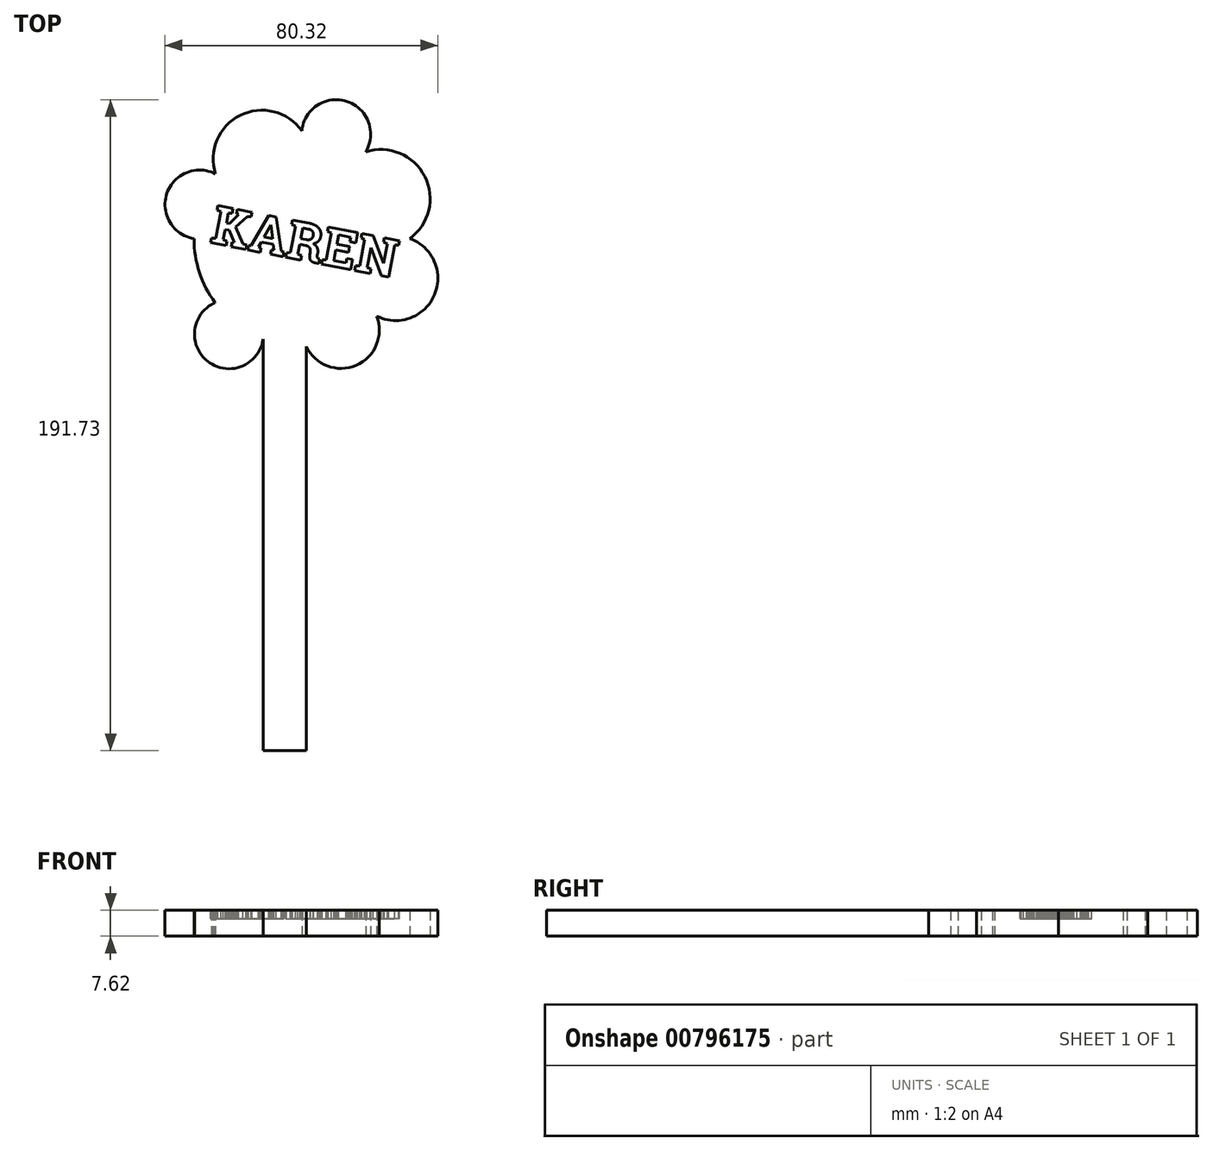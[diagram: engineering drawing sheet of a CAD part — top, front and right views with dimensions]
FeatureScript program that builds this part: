
annotation { "Feature Type Name" : "Feature", "Feature Type Description" : "" }
export const myFeature = defineFeature(function(context is Context, id is Id, definition is map)
    precondition{}
    {
        {
            var Q0;
            Q0=qCreatedBy(makeId("Top.planeOp"),FACE);
            var sketch = newSketch(context, id + "F0", { "sketchPlane" : qUnion([Q0])});
            skLineSegment(sketch, "E0.bottom", {"start": v(-11.4, 1.6) * mm, "end": v(1.3, 1.6) * mm});
            skLineSegment(sketch, "E0.top", {"start": v(-11.4, -150.8) * mm, "end": v(1.3, -150.8) * mm});
            skLineSegment(sketch, "E0.left", {"start": v(-11.4, 1.6) * mm, "end": v(-11.4, -150.8) * mm});
            skLineSegment(sketch, "E0.right", {"start": v(1.3, 1.6) * mm, "end": v(1.3, -150.8) * mm});
            skCircle(sketch, "E1", {"center": v(0, 0) * mm, "radius": 31.75 * mm});
            skArc(sketch, "E2", {"start": v(-25.54, -18.87) * mm, "mid": v(-27.6, -36.25) * mm, "end": v(-11.4, -29.64) * mm});
            skArc(sketch, "E3", {"start": v(-31.75, 0) * mm, "mid": v(-40.33, -13.28) * mm, "end": v(-25.54, -18.87) * mm});
            skArc(sketch, "E4", {"start": v(-25.41, 19.03) * mm, "mid": v(-39.75, 13.24) * mm, "end": v(-31.75, 0) * mm});
            skArc(sketch, "E5", {"start": v(0, 31.75) * mm, "mid": v(-18.16, 36.29) * mm, "end": v(-25.41, 19.03) * mm});
            skArc(sketch, "E6", {"start": v(18.84, 25.56) * mm, "mid": v(13.28, 40.42) * mm, "end": v(0, 31.75) * mm});
            skArc(sketch, "E7", {"start": v(31.75, 0) * mm, "mid": v(36.21, 18.3) * mm, "end": v(18.84, 25.56) * mm});
            skArc(sketch, "E8", {"start": v(1.3, -31.72) * mm, "mid": v(16, -37.3) * mm, "end": v(22.08, -22.82) * mm});
            skArc(sketch, "E9", {"start": v(22.08, -22.82) * mm, "mid": v(39.07, -16.56) * mm, "end": v(31.75, 0) * mm});
            skSolve(sketch);
        }
        {
            var Q0;
            {var subQ0=sQuery(id+"F0.wireOp",EDGE,"E3");var subQ1=sQuery(id+"F0.wireOp",EDGE,"E2");var subQ5=makeQuery(id+"F0.imprint","INTERSECT",VERTEX,{"derivedFrom":[subQ1,subQ0]});Q0=makeQuery(id+"F0.imprint","IMPRINT",FACE,{"disambiguationData":[TD([[makeQuery(id+"F0.imprint","IMPRINT",EDGE,{"disambiguationData":[TD([[subQ5,1.0]])],"derivedFrom":subQ1}),-1.0]])]});}
            var sketch = newSketch(context, id + "F1", { "sketchPlane" : qUnion([Q0])});
            skSolve(sketch);
        }
        {
            var Q0;
            {var subQ0=sQuery(id+"F0.wireOp",EDGE,"E3");var subQ1=sQuery(id+"F0.wireOp",EDGE,"E2");var subQ5=makeQuery(id+"F0.imprint","INTERSECT",VERTEX,{"derivedFrom":[subQ1,subQ0]});Q0=makeQuery(id+"F0.imprint","IMPRINT",FACE,{"disambiguationData":[TD([[makeQuery(id+"F0.imprint","IMPRINT",EDGE,{"disambiguationData":[TD([[subQ5,-1.0]])],"derivedFrom":subQ1}),1.0]])]});}
            var Q1;
            {var subQ0=sQuery(id+"F0.wireOp",EDGE,"E3");var subQ1=sQuery(id+"F0.wireOp",EDGE,"E2");var subQ5=makeQuery(id+"F0.imprint","INTERSECT",VERTEX,{"derivedFrom":[subQ1,subQ0]});Q1=makeQuery(id+"F1.imprint","IMPRINT",FACE,{"disambiguationData":[TD([[makeQuery(id+"F1.imprint","IMPRINT",EDGE,{"derivedFrom":makeQuery(id+"F0.imprint","IMPRINT",EDGE,{"disambiguationData":[TD([[subQ5,1.0]])],"derivedFrom":subQ1})}),-1.0]])]});}
            var Q2;
            {var subQ0=sQuery(id+"F0.wireOp",EDGE,"E4");Q2=makeQuery(id+"F0.imprint","IMPRINT",FACE,{"disambiguationData":[TD([[makeQuery(id+"F0.imprint","IMPRINT",EDGE,{"derivedFrom":subQ0}),1.0]])]});}
            var Q3;
            {var subQ0=sQuery(id+"F0.wireOp",EDGE,"E5");Q3=makeQuery(id+"F0.imprint","IMPRINT",FACE,{"disambiguationData":[TD([[makeQuery(id+"F0.imprint","IMPRINT",EDGE,{"derivedFrom":subQ0}),1.0]])]});}
            var Q4;
            {var subQ0=sQuery(id+"F0.wireOp",EDGE,"E6");Q4=makeQuery(id+"F0.imprint","IMPRINT",FACE,{"disambiguationData":[TD([[makeQuery(id+"F0.imprint","IMPRINT",EDGE,{"derivedFrom":subQ0}),1.0]])]});}
            var Q5;
            {var subQ0=sQuery(id+"F0.wireOp",EDGE,"E7");Q5=makeQuery(id+"F0.imprint","IMPRINT",FACE,{"disambiguationData":[TD([[makeQuery(id+"F0.imprint","IMPRINT",EDGE,{"derivedFrom":subQ0}),1.0]])]});}
            var Q6;
            {var subQ0=sQuery(id+"F0.wireOp",EDGE,"E9");Q6=makeQuery(id+"F0.imprint","IMPRINT",FACE,{"disambiguationData":[TD([[makeQuery(id+"F0.imprint","IMPRINT",EDGE,{"derivedFrom":subQ0}),1.0]])]});}
            var Q7;
            {var subQ0=sQuery(id+"F0.wireOp",EDGE,"E8");Q7=makeQuery(id+"F0.imprint","IMPRINT",FACE,{"disambiguationData":[TD([[makeQuery(id+"F0.imprint","IMPRINT",EDGE,{"derivedFrom":subQ0}),1.0]])]});}
            var Q8;
            {var subQ0=sQuery(id+"F0.wireOp",EDGE,"E0.top");Q8=makeQuery(id+"F0.imprint","IMPRINT",FACE,{"disambiguationData":[TD([[makeQuery(id+"F0.imprint","IMPRINT",EDGE,{"derivedFrom":subQ0}),1.0]])]});}
            var Q9;
            {var subQ0=sQuery(id+"F0.wireOp",EDGE,"E0.bottom");Q9=makeQuery(id+"F0.imprint","IMPRINT",FACE,{"disambiguationData":[TD([[makeQuery(id+"F0.imprint","IMPRINT",EDGE,{"derivedFrom":subQ0}),-1.0]])]});}
            var Q10;
            {var subQ14=sQuery(id+"F0.wireOp",EDGE,"E0.bottom");Q10=makeQuery(id+"F0.imprint","IMPRINT",FACE,{"disambiguationData":[TD([[makeQuery(id+"F0.imprint","IMPRINT",EDGE,{"derivedFrom":subQ14}),1.0]])]});}
            extrude(context, id + "F2", {"entities" : qUnion([Q0, Q1, Q2, Q3, Q4, Q5, Q6, Q7, Q8, Q9, Q10]), "depth" : 7.62 * mm, "offsetDistance" : 25.4 * mm});
        }
        {
            var Q0;
            Q0=makeQuery(id+"F2.opExtrude","CAP_FACE",FACE,{"disambiguationData":[OSD([sQuery(id+"F0.wireOp",EDGE,"E0.top"),sQuery(id+"F0.wireOp",EDGE,"E0.left"),sQuery(id+"F0.wireOp",EDGE,"E0.right"),sQuery(id+"F0.wireOp",EDGE,"E1"),sQuery(id+"F0.wireOp",EDGE,"E2"),sQuery(id+"F0.wireOp",EDGE,"E3"),sQuery(id+"F0.wireOp",EDGE,"E4"),sQuery(id+"F0.wireOp",EDGE,"E5"),sQuery(id+"F0.wireOp",EDGE,"E6"),sQuery(id+"F0.wireOp",EDGE,"E7"),sQuery(id+"F0.wireOp",EDGE,"E8"),sQuery(id+"F0.wireOp",EDGE,"E9")])],"isStart":false});
            var sketch = newSketch(context, id + "F3", { "sketchPlane" : qUnion([Q0])});
            skText(sketch, "E10", { "text": "KAREN\n", "fontName": "RobotoSlab-Bold.ttf"});
            const initialGuessF3  = {"E10": [-0.02723, -0.00113, 0.98191, -0.18932, 0.01126]};
            skSetInitialGuess(sketch, initialGuessF3);
            skSolve(sketch);
        }
        {
            var Q0;
            Q0 = qSketchRegion(id + "F3", true);
            extrude(context, id + "F4", {"entities" : qUnion([Q0]), "operationType" : NewBodyOperationType.REMOVE, "oppositeDirection" : true, "depth" : 2.54 * mm, "offsetDistance" : 25.4 * mm});
        }
    });
